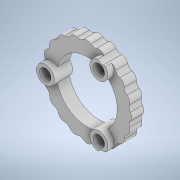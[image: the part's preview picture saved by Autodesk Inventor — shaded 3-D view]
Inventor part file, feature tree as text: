
AUTODESK INVENTOR PART (.ipt)
format: ipt  version: 2022 (Build 260153000, 153)  size: 483,328 bytes
history: native  units: in
note: dims shown in document units (in); Inventor stores cm internally (conversion verified against a paired STEP export)
features: sketch x8, projected_geometry x8, extrude x7, thicken_offset x6, other x6, plane x1, fillet x1, reference x1
ambient origin geometry x8: Origin, YZ Plane, XZ Plane, XY Plane, X Axis, Y Axis, Z Axis, Center Point
bodies: Solid1 (feature_tree)
feature tree (38):
  extrude  "Extrusion1"  Depth=1.1681in
  plane  "Work Plane1"
  extrude  "Extrusion2"  Depth=0.481in
  extrude  "Extrusion3"  Depth=0.481in
  thicken_offset  "Thicken1"
  thicken_offset  "Thicken2"
  thicken_offset  "Thicken3"
  extrude  "Extrusion4"  Depth=0.6in TaperAngle=0.0deg
  fillet  "Fillet1"  Radius=1.315in
  thicken_offset  "Thicken4"
  thicken_offset  "Thicken5"
  thicken_offset  "Thicken6"
  sketch  "Sketch6"  dims[d8=1.1681in d9=1.1681in d10=0.3436in d11=0.481in d12=0.3436in d13=0.481in d14=0.6in d15=0.0in d16=1.315in]
  extrude  "Extrusion5"  Depth=0.1181in
  extrude  "Extrusion6"  Depth=0.1181in
  extrude  "Extrusion7"  Depth=0.25in
  sketch  "Sketch1"  dims[d0=1.1681in d1=1.1681in]
  reference  "Reference1"
  sketch  "Sketch3"  dims[d2=0.3436in d3=0.481in]
  sketch  "Sketch4"  dims[d4=0.3436in d5=0.481in]
  projected_geometry  "Projected Loop1"
  projected_geometry  "Projected Loop2"
  projected_geometry  "Projected Loop3"
  sketch  "Sketch5"  dims[d6=0.2in d7=0.0in]
  projected_geometry  "Projected Loop4"
  projected_geometry  "Projected Loop8"
  sketch  "Sketch8"  dims[d17=1.025in d18=0.1181in]
  projected_geometry  "Projected Loop9"
  sketch  "Sketch9"  dims[d19=0.1181in d20=0.1181in]
  sketch  "Sketch10"  dims[d21=0.25in d22=0.0in d26=0.005in d27=0.005in d28=0.005in d29=0.005in d30=0.005in d31=0.005in d32=0.1in d33=135.0deg d34=45.0deg d35=7.874in d37=360.0deg d39=0.2in d40=0.0in d41=0.1in d42=0.01in d43=0.01in d44=0.01in d45=0.01in d46=0.01in d47=0.01in d48=0.189in d49=0.189in d50=0.189in d51=0.3718in d52=0.3in d53=0.3in d54=0.3in d55=0.1in d56=0.0in d57=0.3in d58=0.3in d59=0.3in d60=0.1in d61=0.0in d62=0.25in d63=0.0in]
  projected_geometry  "Projected Loop10"
  projected_geometry  "Projected Loop11"
  parser-record x2  (decoder bookkeeping rows leaked as tree rows — omitted from the tree; the rows remain in map.json)
  other  "CubeAssembly.iam"
  other  "CubeFace:2"
  other  "Assembly1.iam"
  other  "CubeFace:1"
note: 2 file-system paths scrubbed to <path> (originals preserved in map.json)
